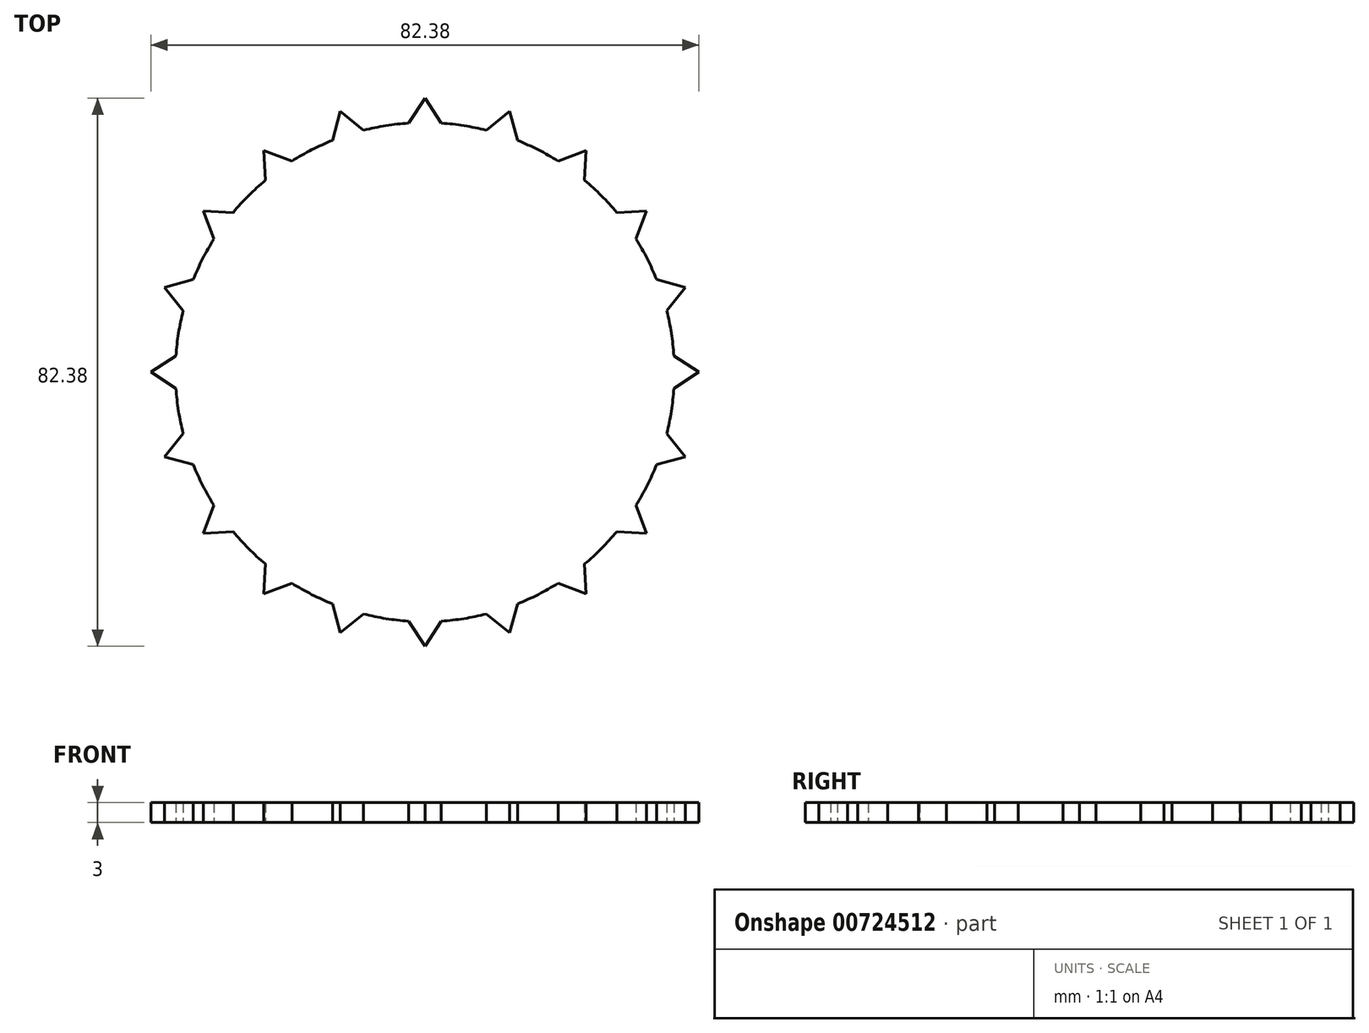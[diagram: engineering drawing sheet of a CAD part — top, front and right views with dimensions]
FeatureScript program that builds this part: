
annotation { "Feature Type Name" : "Feature", "Feature Type Description" : "" }
export const myFeature = defineFeature(function(context is Context, id is Id, definition is map)
    precondition{}
    {
        {
            var Q0;
            Q0=qCreatedBy(makeId("Top.planeOp"),FACE);
            var sketch = newSketch(context, id + "F0", { "sketchPlane" : qUnion([Q0])});
            skCircle(sketch, "E0", {"center": v(0, 0) * mm, "radius": 37.5 * mm});
            skLineSegment(sketch, "E1", {"start": v(-2.47, 37.42) * mm, "end": v(0, 41.19) * mm});
            skLineSegment(sketch, "E2", {"start": v(0, 41.19) * mm, "end": v(2.47, 37.42) * mm});
            skLineSegment(sketch, "E3.1.0", {"start": v(-12.73, 39.17) * mm, "end": v(-9.22, 36.35) * mm});
            skLineSegment(sketch, "E3.1.1", {"start": v(-13.9, 34.83) * mm, "end": v(-12.73, 39.17) * mm});
            skLineSegment(sketch, "E3.2.0", {"start": v(-24.2, 33.32) * mm, "end": v(-20, 31.72) * mm});
            skLineSegment(sketch, "E3.2.1", {"start": v(-23.99, 28.82) * mm, "end": v(-24.2, 33.32) * mm});
            skLineSegment(sketch, "E3.3.0", {"start": v(-33.32, 24.2) * mm, "end": v(-28.82, 23.99) * mm});
            skLineSegment(sketch, "E3.3.1", {"start": v(-31.72, 20) * mm, "end": v(-33.32, 24.2) * mm});
            skLineSegment(sketch, "E3.4.0", {"start": v(-39.17, 12.73) * mm, "end": v(-34.83, 13.9) * mm});
            skLineSegment(sketch, "E3.4.1", {"start": v(-36.35, 9.22) * mm, "end": v(-39.17, 12.73) * mm});
            skLineSegment(sketch, "E3.5.0", {"start": v(-41.19, 0) * mm, "end": v(-37.42, 2.47) * mm});
            skLineSegment(sketch, "E3.5.1", {"start": v(-37.42, -2.47) * mm, "end": v(-41.19, 0) * mm});
            skLineSegment(sketch, "E3.6.0", {"start": v(-39.17, -12.73) * mm, "end": v(-36.35, -9.22) * mm});
            skLineSegment(sketch, "E3.6.1", {"start": v(-34.83, -13.9) * mm, "end": v(-39.17, -12.73) * mm});
            skLineSegment(sketch, "E3.7.0", {"start": v(-33.32, -24.2) * mm, "end": v(-31.72, -20) * mm});
            skLineSegment(sketch, "E3.7.1", {"start": v(-28.82, -23.99) * mm, "end": v(-33.32, -24.2) * mm});
            skLineSegment(sketch, "E3.8.0", {"start": v(-24.2, -33.32) * mm, "end": v(-23.99, -28.82) * mm});
            skLineSegment(sketch, "E3.8.1", {"start": v(-20, -31.72) * mm, "end": v(-24.2, -33.32) * mm});
            skLineSegment(sketch, "E3.9.0", {"start": v(-12.73, -39.17) * mm, "end": v(-13.9, -34.83) * mm});
            skLineSegment(sketch, "E3.9.1", {"start": v(-9.22, -36.35) * mm, "end": v(-12.73, -39.17) * mm});
            skLineSegment(sketch, "E3.10.0", {"start": v(0, -41.19) * mm, "end": v(-2.47, -37.42) * mm});
            skLineSegment(sketch, "E3.10.1", {"start": v(2.47, -37.42) * mm, "end": v(0, -41.19) * mm});
            skLineSegment(sketch, "E3.11.0", {"start": v(12.73, -39.17) * mm, "end": v(9.22, -36.35) * mm});
            skLineSegment(sketch, "E3.11.1", {"start": v(13.9, -34.83) * mm, "end": v(12.73, -39.17) * mm});
            skLineSegment(sketch, "E3.12.0", {"start": v(24.2, -33.32) * mm, "end": v(20, -31.72) * mm});
            skLineSegment(sketch, "E3.12.1", {"start": v(23.99, -28.82) * mm, "end": v(24.2, -33.32) * mm});
            skLineSegment(sketch, "E3.13.0", {"start": v(33.32, -24.2) * mm, "end": v(28.82, -23.99) * mm});
            skLineSegment(sketch, "E3.13.1", {"start": v(31.72, -20) * mm, "end": v(33.32, -24.2) * mm});
            skLineSegment(sketch, "E3.14.0", {"start": v(39.17, -12.73) * mm, "end": v(34.83, -13.9) * mm});
            skLineSegment(sketch, "E3.14.1", {"start": v(36.35, -9.22) * mm, "end": v(39.17, -12.73) * mm});
            skLineSegment(sketch, "E3.15.0", {"start": v(41.19, 0) * mm, "end": v(37.42, -2.47) * mm});
            skLineSegment(sketch, "E3.15.1", {"start": v(37.42, 2.47) * mm, "end": v(41.19, 0) * mm});
            skLineSegment(sketch, "E3.16.0", {"start": v(39.17, 12.73) * mm, "end": v(36.35, 9.22) * mm});
            skLineSegment(sketch, "E3.16.1", {"start": v(34.83, 13.9) * mm, "end": v(39.17, 12.73) * mm});
            skLineSegment(sketch, "E3.17.0", {"start": v(33.32, 24.2) * mm, "end": v(31.72, 20) * mm});
            skLineSegment(sketch, "E3.17.1", {"start": v(28.82, 23.99) * mm, "end": v(33.32, 24.2) * mm});
            skLineSegment(sketch, "E3.18.0", {"start": v(24.2, 33.32) * mm, "end": v(23.99, 28.82) * mm});
            skLineSegment(sketch, "E3.18.1", {"start": v(20, 31.72) * mm, "end": v(24.2, 33.32) * mm});
            skLineSegment(sketch, "E3.19.0", {"start": v(12.73, 39.17) * mm, "end": v(13.9, 34.83) * mm});
            skLineSegment(sketch, "E3.19.1", {"start": v(9.22, 36.35) * mm, "end": v(12.73, 39.17) * mm});
            skSolve(sketch);
        }
        {
            var Q0;
            Q0=qSketchRegion(id+"F0",true);
            extrude(context, id + "F1", {"entities" : qUnion([Q0]), "depth" : 3 * mm, "offsetDistance" : 25 * mm});
        }
    });
